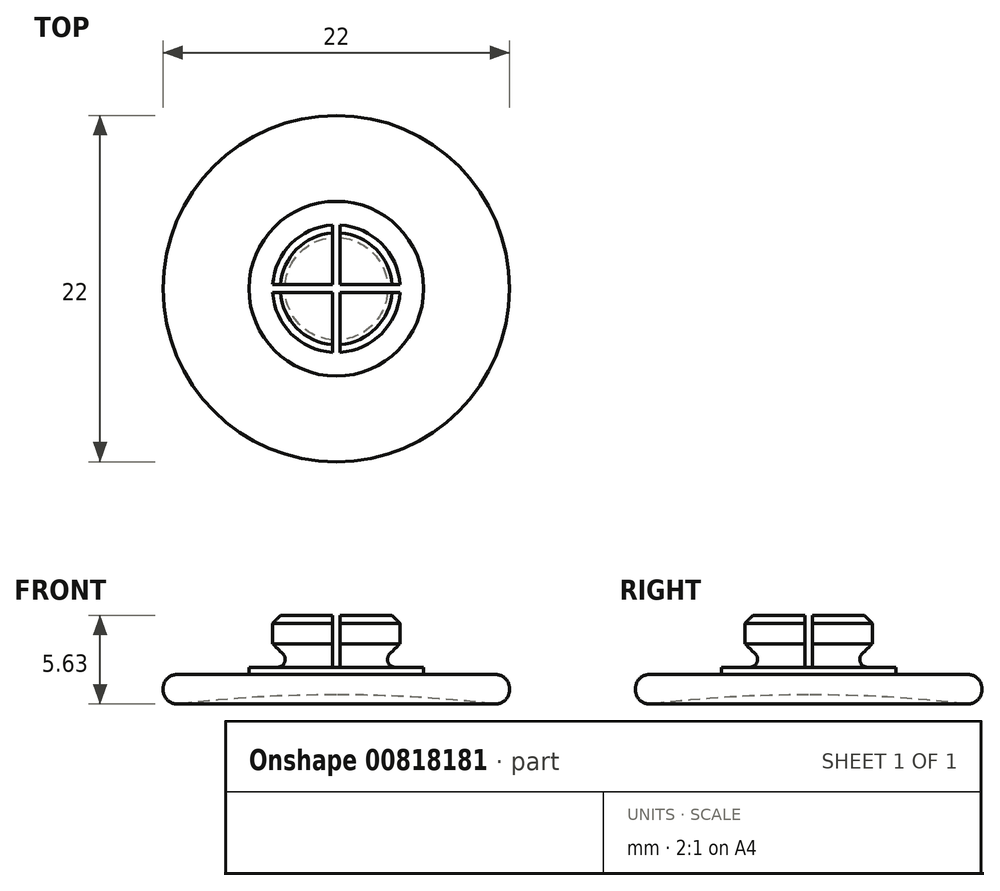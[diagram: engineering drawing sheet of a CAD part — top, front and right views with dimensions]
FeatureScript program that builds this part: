
annotation { "Feature Type Name" : "Feature", "Feature Type Description" : "" }
export const myFeature = defineFeature(function(context is Context, id is Id, definition is map)
    precondition{}
    {
        {
            var Q0;
            Q0=qCreatedBy(makeId("Front.planeOp"),FACE);
            var sketch = newSketch(context, id + "F0", { "sketchPlane" : qUnion([Q0])});
            skLineSegment(sketch, "E0", {"start": v(0, 0) * mm, "end": v(11, 0) * mm, "construction": true});
            skLineSegment(sketch, "E1", {"start": v(11, 0) * mm, "end": v(11, 2) * mm});
            skLineSegment(sketch, "E2", {"start": v(11, 2) * mm, "end": v(5.55, 2) * mm});
            skLineSegment(sketch, "E3", {"start": v(5.55, 2) * mm, "end": v(5.55, 2.45) * mm});
            skLineSegment(sketch, "E4", {"start": v(4.05, 3.95) * mm, "end": v(4.05, 5.75) * mm});
            skLineSegment(sketch, "E5", {"start": v(4.05, 5.75) * mm, "end": v(0, 5.75) * mm});
            skLineSegment(sketch, "E6", {"start": v(0, 5.75) * mm, "end": v(0, 0.7) * mm});
            skLineSegment(sketch, "E7", {"start": v(5.55, 2.45) * mm, "end": v(2.55, 2.45) * mm});
            skPoint(sketch, "E8.orphan", {"position": v(2.55, 1.8) * mm});
            skLineSegment(sketch, "E9", {"start": v(2.55, 2.45) * mm, "end": v(4.05, 3.95) * mm});
            skPoint(sketch, "E10.end.orphan", {"position": v(2.55, 3.1) * mm});
            skArc(sketch, "E11", {"start": v(11, 0) * mm, "mid": v(5.51, 0.52) * mm, "end": v(0, 0.7) * mm});
            skSolve(sketch);
        }
        {
            var Q0;
            Q0=makeQuery(id+"F0.imprint","IMPRINT",FACE,{"disambiguationData":[TD([[makeQuery(id+"F0.imprint","IMPRINT",EDGE,{"derivedFrom":sQuery(id+"F0.wireOp",EDGE,"E1")}),1.0]])]});
            var Q1;
            Q1=sQuery(id+"F0.wireOp",EDGE,"E6");
            revolve(context, id + "F1", {"surfaceOperationType" : NewSurfaceOperationType.NEW, "entities" : qUnion([Q0]), "axis" : qUnion([Q1]), "revolveType" : RevolveType.FULL});
        }
        {
            var Q0;
            Q0=makeQuery(id+"F1.opRevolve","SWEPT_EDGE",EDGE,{"disambiguationData":[OSD([sQuery(id+"F0.wireOp",EDGE,"E7"),sQuery(id+"F0.wireOp",EDGE,"E9")])]});
            fillet(context, id + "F2", {"entities" : qUnion([Q0]), "radius" : 0.5 * mm, "tangentPropagation" : true, "allowEdgeOverflow" : false});
        }
        {
            var Q0;
            Q0=makeQuery(id+"F1.opRevolve","SWEPT_EDGE",EDGE,{"disambiguationData":[OSD([sQuery(id+"F0.wireOp",EDGE,"E0"),sQuery(id+"F0.wireOp",EDGE,"E1")])]});
            var Q1;
            Q1=makeQuery(id+"F1.opRevolve","SWEPT_EDGE",EDGE,{"disambiguationData":[OSD([sQuery(id+"F0.wireOp",EDGE,"E1"),sQuery(id+"F0.wireOp",EDGE,"E2")])]});
            fillet(context, id + "F3", {"entities" : qUnion([Q0, Q1]), "radius" : 0.9 * mm, "tangentPropagation" : true, "allowEdgeOverflow" : false});
        }
        {
            var Q0;
            Q0=makeQuery(id+"F1.opRevolve","SWEPT_FACE",FACE,{"disambiguationData":[OSD([sQuery(id+"F0.wireOp",EDGE,"E5")])]});
            chamfer(context, id + "F4", {"entities" : qUnion([Q0]), "width" : 0.5 * mm, "tangentPropagation" : true});
        }
        {
            var Q0;
            Q0=makeQuery(id+"F1.opRevolve","SWEPT_FACE",FACE,{"disambiguationData":[OSD([sQuery(id+"F0.wireOp",EDGE,"E5")])]});
            var sketch = newSketch(context, id + "F5", { "sketchPlane" : qUnion([Q0])});
            skLineSegment(sketch, "E12.bottom", {"start": v(-0.25, 4.5) * mm, "end": v(0.25, 4.5) * mm});
            skLineSegment(sketch, "E12.top", {"start": v(-0.25, -4.5) * mm, "end": v(0.25, -4.5) * mm});
            skLineSegment(sketch, "E12.left", {"start": v(-0.25, 4.5) * mm, "end": v(-0.25, 0.25) * mm});
            skLineSegment(sketch, "E12.right", {"start": v(0.25, 4.5) * mm, "end": v(0.25, 0.25) * mm});
            skLineSegment(sketch, "E13.bottom", {"start": v(-4.5, 0.25) * mm, "end": v(-0.25, 0.25) * mm});
            skLineSegment(sketch, "E13.top", {"start": v(-4.5, -0.25) * mm, "end": v(-0.25, -0.25) * mm});
            skLineSegment(sketch, "E13.left", {"start": v(-4.5, 0.25) * mm, "end": v(-4.5, -0.25) * mm});
            skLineSegment(sketch, "E13.right", {"start": v(4.5, 0.25) * mm, "end": v(4.5, -0.25) * mm});
            skLineSegment(sketch, "E14.trimOffspring", {"start": v(-0.25, -0.25) * mm, "end": v(-0.25, -4.5) * mm});
            skLineSegment(sketch, "E15.trimOffspring", {"start": v(0.25, 0.25) * mm, "end": v(4.5, 0.25) * mm});
            skLineSegment(sketch, "E16.trimOffspring", {"start": v(0.25, -0.25) * mm, "end": v(4.5, -0.25) * mm});
            skLineSegment(sketch, "E17.trimOffspring", {"start": v(0.25, -0.25) * mm, "end": v(0.25, -4.5) * mm});
            skLineSegment(sketch, "E18", {"start": v(0, 4.5) * mm, "end": v(0, 0) * mm, "construction": true});
            skLineSegment(sketch, "E19", {"start": v(0, 0) * mm, "end": v(-4.5, 0) * mm, "construction": true});
            skSolve(sketch);
        }
        {
            var Q0;
            Q0 = qSketchRegion(id + "F5", true);
            var Q1;
            Q1=makeQuery(id+"F1.opRevolve","SWEPT_FACE",FACE,{"disambiguationData":[OSD([sQuery(id+"F0.wireOp",EDGE,"E7")])]});
            extrude(context, id + "F6", {"entities" : qUnion([Q0]), "operationType" : NewBodyOperationType.REMOVE, "endBound" : BoundingType.UP_TO_SURFACE, "oppositeDirection" : true, "depth" : 25 * mm, "endBoundEntityFace" : qUnion([Q1]), "offsetDistance" : 25 * mm});
        }
    });
